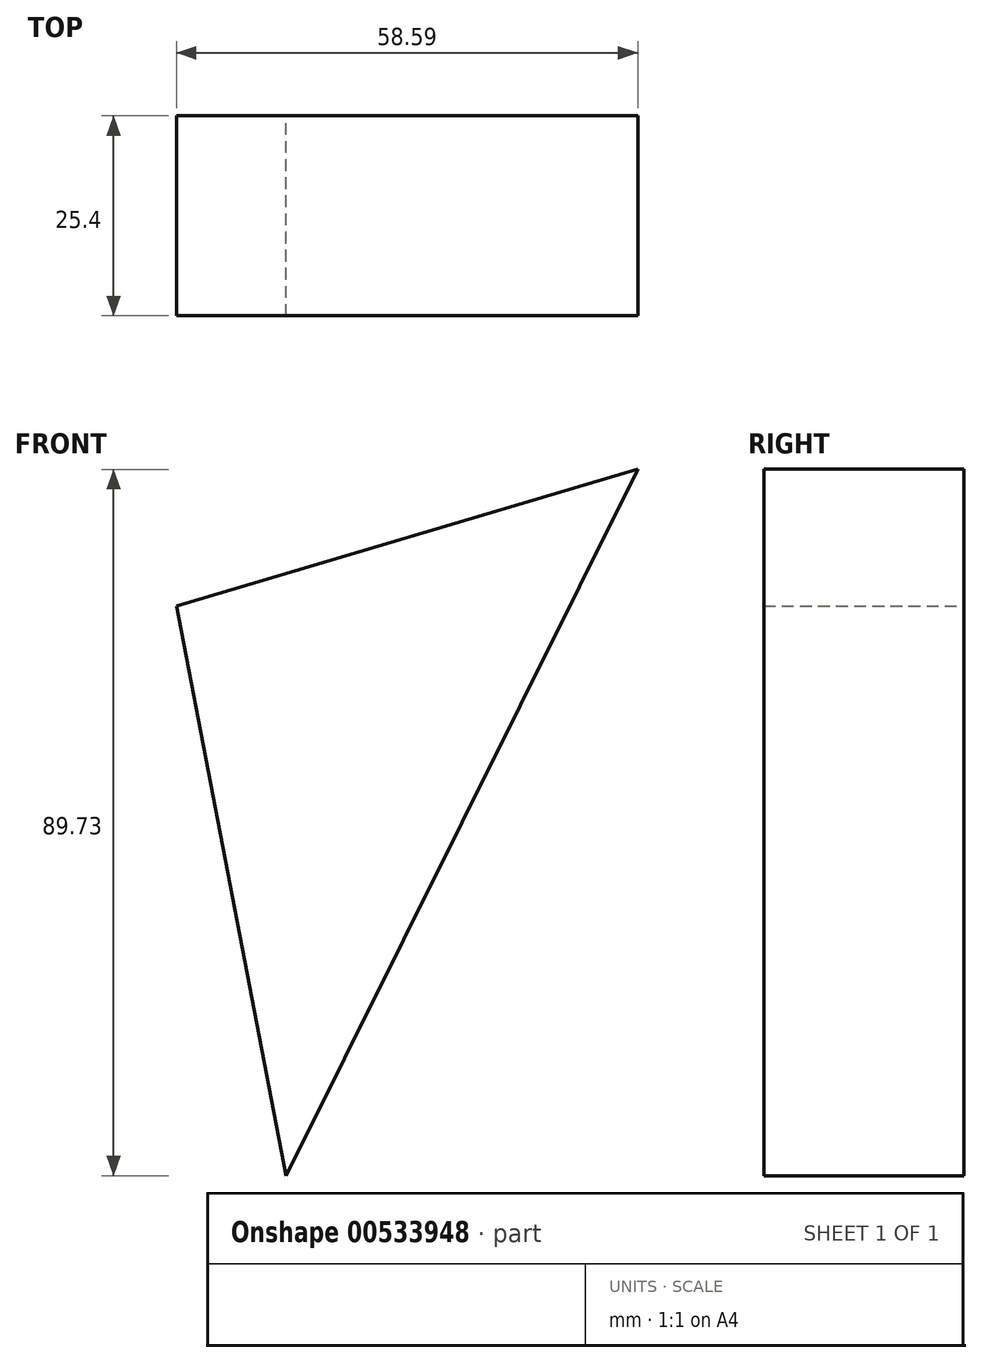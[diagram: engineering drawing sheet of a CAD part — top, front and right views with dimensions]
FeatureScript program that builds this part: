
annotation { "Feature Type Name" : "Feature", "Feature Type Description" : "" }
export const myFeature = defineFeature(function(context is Context, id is Id, definition is map)
    precondition{}
    {
        {
            var Q0;
            Q0=qCreatedBy(makeId("Front.planeOp"),FACE);
            var sketch = newSketch(context, id + "F0", { "sketchPlane" : qUnion([Q0])});
            skLineSegment(sketch, "E0", {"start": v(-91.25, 59.62) * mm, "end": v(-135.9, -30.1) * mm});
            skLineSegment(sketch, "E1", {"start": v(-149.84, 42.23) * mm, "end": v(-135.9, -30.1) * mm});
            skLineSegment(sketch, "E2", {"start": v(-149.84, 42.23) * mm, "end": v(-91.25, 59.62) * mm});
            skSolve(sketch);
        }
        {
            var Q0;
            Q0 = qSketchRegion(id + "F0", true);
            var Q1;
            Q1=makeQuery(id+"F0.imprint","IMPRINT",FACE,{"disambiguationData":[TD([[makeQuery(id+"F0.imprint","IMPRINT",EDGE,{"derivedFrom":sQuery(id+"F0.wireOp",EDGE,"E0")}),-1.0]])]});
            extrude(context, id + "F1", {"entities" : qUnion([Q0, Q1]), "depth" : 25.4 * mm, "offsetDistance" : 25.4 * mm});
        }
    });
